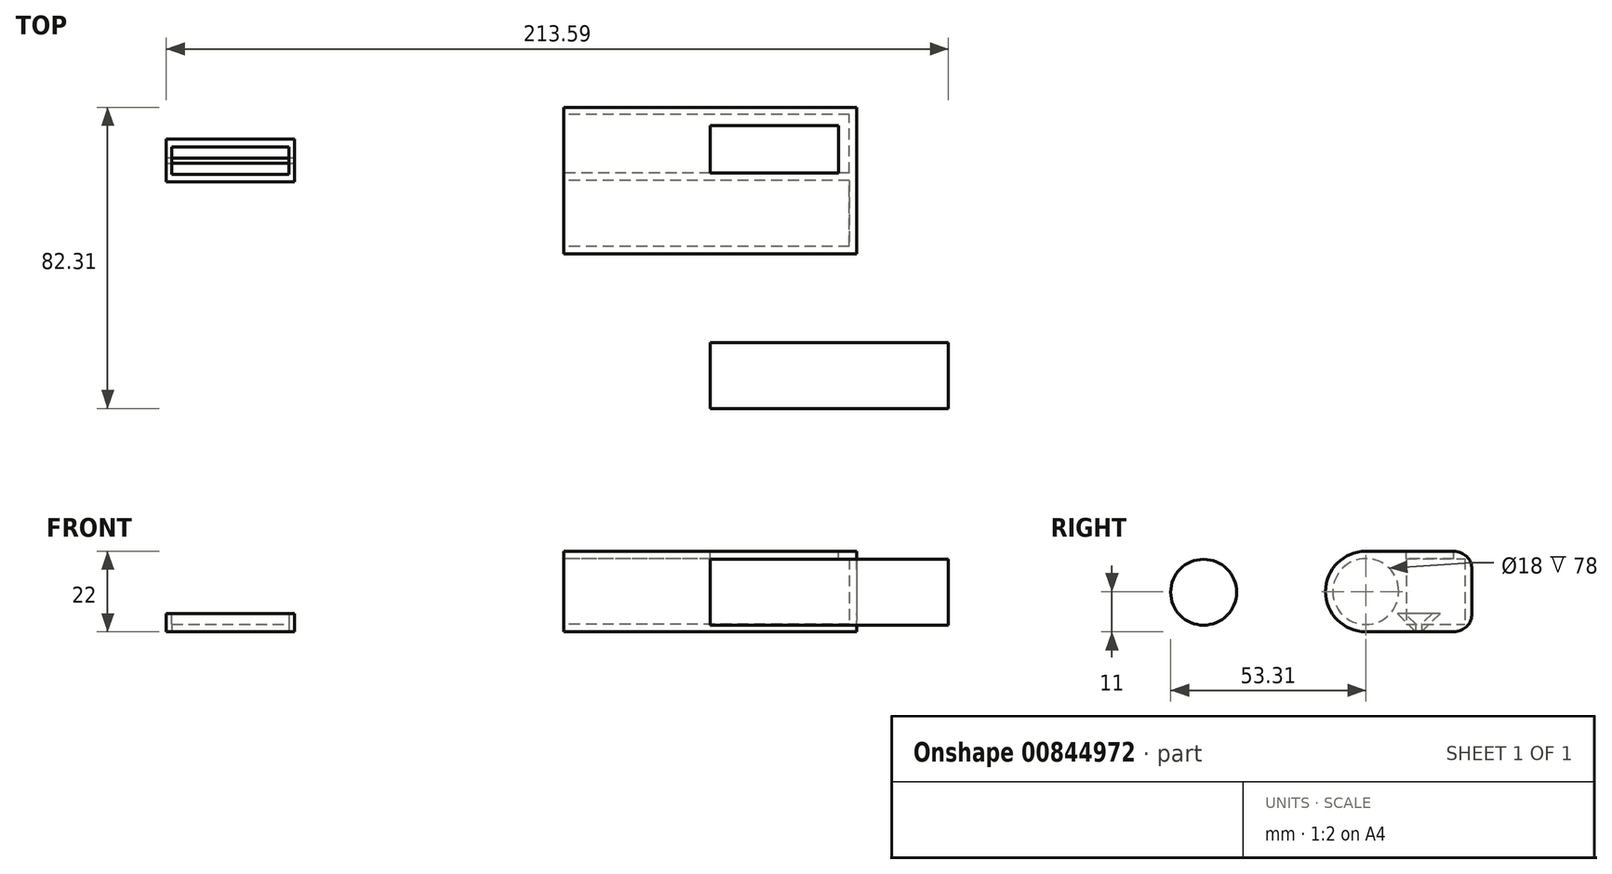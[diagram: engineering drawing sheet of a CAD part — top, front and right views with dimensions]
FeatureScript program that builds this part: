
annotation { "Feature Type Name" : "Feature", "Feature Type Description" : "" }
export const myFeature = defineFeature(function(context is Context, id is Id, definition is map)
    precondition{}
    {
        {
            var Q0;
            Q0=qCreatedBy(makeId("Top.planeOp"),FACE);
            var sketch = newSketch(context, id + "F0", { "sketchPlane" : qUnion([Q0])});
            skLineSegment(sketch, "E0.bottom", {"start": v(40, 20) * mm, "end": v(-40, 20) * mm});
            skLineSegment(sketch, "E0.top", {"start": v(40, -20) * mm, "end": v(-40, -20) * mm});
            skLineSegment(sketch, "E0.left", {"start": v(40, 20) * mm, "end": v(40, -20) * mm});
            skLineSegment(sketch, "E0.right", {"start": v(-40, 20) * mm, "end": v(-40, -20) * mm});
            skPoint(sketch, "E0.middle", {"position": v(0, 0) * mm});
            skSolve(sketch);
        }
        {
            var Q0;
            Q0=makeQuery(id+"F0.imprint","IMPRINT",FACE,{"disambiguationData":[TD([[makeQuery(id+"F0.imprint","IMPRINT",EDGE,{"derivedFrom":sQuery(id+"F0.wireOp",EDGE,"E0.bottom")}),1.0]])]});
            extrude(context, id + "F1", {"entities" : qUnion([Q0]), "depth" : 22 * mm, "offsetDistance" : 25.4 * mm});
        }
        {
            var Q0;
            Q0=makeQuery(id+"F1.opExtrude","CAP_EDGE",EDGE,{"disambiguationData":[OSD([sQuery(id+"F0.wireOp",EDGE,"E0.top")])],"isStart":false});
            var Q1;
            Q1=makeQuery(id+"F1.opExtrude","CAP_EDGE",EDGE,{"disambiguationData":[OSD([sQuery(id+"F0.wireOp",EDGE,"E0.top")])],"isStart":true});
            fillet(context, id + "F2", {"entities" : qUnion([Q0, Q1]), "radius" : 11 * mm, "tangentPropagation" : true, "allowEdgeOverflow" : false});
        }
        {
            var Q0;
            Q0=makeQuery(id+"F1.opExtrude","CAP_FACE",FACE,{"disambiguationData":[OSD([sQuery(id+"F0.wireOp",EDGE,"E0.bottom"),sQuery(id+"F0.wireOp",EDGE,"E0.top"),sQuery(id+"F0.wireOp",EDGE,"E0.left"),sQuery(id+"F0.wireOp",EDGE,"E0.right")])],"isStart":false});
            var sketch = newSketch(context, id + "F3", { "sketchPlane" : qUnion([Q0])});
            skLineSegment(sketch, "E1.bottom", {"start": v(35, 15) * mm, "end": v(0, 15) * mm});
            skLineSegment(sketch, "E1.top", {"start": v(35, 2) * mm, "end": v(0, 2) * mm});
            skLineSegment(sketch, "E1.left", {"start": v(35, 15) * mm, "end": v(35, 2) * mm});
            skLineSegment(sketch, "E1.right", {"start": v(0, 15) * mm, "end": v(0, 2) * mm});
            skPoint(sketch, "E1.middle", {"position": v(17.5, 8.5) * mm});
            skSolve(sketch);
        }
        {
            var Q0;
            Q0 = qSketchRegion(id + "F3", true);
            extrude(context, id + "F4", {"entities" : qUnion([Q0]), "operationType" : NewBodyOperationType.REMOVE, "oppositeDirection" : true, "depth" : 2 * mm, "offsetDistance" : 25.4 * mm});
        }
        {
            var Q0;
            Q0=makeQuery(id+"F1.opExtrude","CAP_EDGE",EDGE,{"disambiguationData":[OSD([sQuery(id+"F0.wireOp",EDGE,"E0.bottom")])],"isStart":false});
            var Q1;
            Q1=makeQuery(id+"F1.opExtrude","CAP_EDGE",EDGE,{"disambiguationData":[OSD([sQuery(id+"F0.wireOp",EDGE,"E0.bottom")])],"isStart":true});
            fillet(context, id + "F5", {"entities" : qUnion([Q0, Q1]), "radius" : 5 * mm, "tangentPropagation" : true, "allowEdgeOverflow" : false});
        }
        {
            var Q0;
            Q0=qCreatedBy(makeId("Top.planeOp"),FACE);
            var sketch = newSketch(context, id + "F6", { "sketchPlane" : qUnion([Q0])});
            skLineSegment(sketch, "E2.bottom", {"start": v(-113.6, 11.36) * mm, "end": v(-148.6, 11.36) * mm});
            skLineSegment(sketch, "E2.top", {"start": v(-113.6, -0.5) * mm, "end": v(-148.6, -0.5) * mm});
            skLineSegment(sketch, "E2.left", {"start": v(-113.6, 11.36) * mm, "end": v(-113.6, -0.5) * mm});
            skLineSegment(sketch, "E2.right", {"start": v(-148.6, 11.36) * mm, "end": v(-148.6, -0.5) * mm});
            skPoint(sketch, "E2.middle", {"position": v(-131.1, 5.43) * mm});
            skSolve(sketch);
        }
        {
            var Q0;
            Q0=makeQuery(id+"F6.imprint","IMPRINT",FACE,{"disambiguationData":[TD([[makeQuery(id+"F6.imprint","IMPRINT",EDGE,{"derivedFrom":sQuery(id+"F6.wireOp",EDGE,"E2.bottom")}),1.0]])]});
            extrude(context, id + "F7", {"entities" : qUnion([Q0]), "depth" : 5 * mm, "offsetDistance" : 25.4 * mm});
        }
        {
            var Q0;
            Q0=makeQuery(id+"F7.opExtrude","CAP_EDGE",EDGE,{"disambiguationData":[OSD([sQuery(id+"F6.wireOp",EDGE,"E2.top")])],"isStart":true});
            var Q1;
            Q1=makeQuery(id+"F7.opExtrude","CAP_EDGE",EDGE,{"disambiguationData":[OSD([sQuery(id+"F6.wireOp",EDGE,"E2.bottom")])],"isStart":true});
            chamfer(context, id + "F8", {"entities" : qUnion([Q0, Q1]), "width" : 5.08 * mm});
        }
        {
            var Q0;
            Q0=makeQuery(id+"F7.opExtrude","CAP_FACE",FACE,{"disambiguationData":[OSD([sQuery(id+"F6.wireOp",EDGE,"E2.bottom"),sQuery(id+"F6.wireOp",EDGE,"E2.top"),sQuery(id+"F6.wireOp",EDGE,"E2.left"),sQuery(id+"F6.wireOp",EDGE,"E2.right")])],"isStart":false});
            shell(context, id + "F9", {"entities" : qUnion([Q0]), "thickness" : 1.5 * mm});
        }
        {
            var Q0;
            Q0=makeQuery(id+"F7.opExtrude","CAP_FACE",FACE,{"disambiguationData":[OSD([sQuery(id+"F6.wireOp",EDGE,"E2.bottom"),sQuery(id+"F6.wireOp",EDGE,"E2.top"),sQuery(id+"F6.wireOp",EDGE,"E2.left"),sQuery(id+"F6.wireOp",EDGE,"E2.right")])],"isStart":true});
            var sketch = newSketch(context, id + "F10", { "sketchPlane" : qUnion([Q0])});
            skLineSegment(sketch, "E3.bottom", {"start": v(-115.1, -6.28) * mm, "end": v(-147.1, -6.28) * mm});
            skLineSegment(sketch, "E3.top", {"start": v(-115.1, -4.58) * mm, "end": v(-147.1, -4.58) * mm});
            skLineSegment(sketch, "E3.left", {"start": v(-115.1, -6.28) * mm, "end": v(-115.1, -4.58) * mm});
            skLineSegment(sketch, "E3.right", {"start": v(-147.1, -6.28) * mm, "end": v(-147.1, -4.58) * mm});
            skPoint(sketch, "E3.middle", {"position": v(-131.1, -5.43) * mm});
            skPoint(sketch, "E3.middle.positionSnap0", {"position": v(-131.1, -6.28) * mm});
            skPoint(sketch, "E3.centerSnap0", {"position": v(-131.1, -6.28) * mm});
            skSolve(sketch);
        }
        {
            var Q0;
            Q0 = qSketchRegion(id + "F10", true);
            extrude(context, id + "F11", {"entities" : qUnion([Q0]), "operationType" : NewBodyOperationType.REMOVE, "oppositeDirection" : true, "depth" : 2 * mm, "offsetDistance" : 25.4 * mm});
        }
        {
            var Q0;
            Q0=qCreatedBy(makeId("Right.planeOp"),FACE);
            var sketch = newSketch(context, id + "F12", { "sketchPlane" : qUnion([Q0])});
            skCircle(sketch, "E4", {"center": v(-53.3, 10.8) * mm, "radius": 9 * mm});
            skSolve(sketch);
        }
        {
            var Q0;
            Q0 = qSketchRegion(id + "F12", true);
            extrude(context, id + "F13", {"entities" : qUnion([Q0]), "depth" : 65 * mm, "offsetDistance" : 25.4 * mm});
        }
        {
            var Q0;
            Q0=makeQuery(id+"F1.opExtrude","SWEPT_FACE",FACE,{"disambiguationData":[OSD([sQuery(id+"F0.wireOp",EDGE,"E0.right")])]});
            var sketch = newSketch(context, id + "F14", { "sketchPlane" : qUnion([Q0])});
            skCircle(sketch, "E5", {"center": v(9, 11) * mm, "radius": 9 * mm});
            skSolve(sketch);
        }
        {
            var Q0;
            Q0=makeQuery(id+"F14.imprint","IMPRINT",FACE,{"disambiguationData":[TD([[makeQuery(id+"F14.imprint","IMPRINT",EDGE,{"derivedFrom":sQuery(id+"F14.wireOp",EDGE,"E5")}),1.0]])]});
            extrude(context, id + "F15", {"entities" : qUnion([Q0]), "operationType" : NewBodyOperationType.REMOVE, "oppositeDirection" : true, "depth" : 78 * mm, "offsetDistance" : 25.4 * mm});
        }
        {
            var Q0;
            Q0=makeQuery(id+"F1.opExtrude","SWEPT_FACE",FACE,{"disambiguationData":[OSD([sQuery(id+"F0.wireOp",EDGE,"E0.right")])]});
            var sketch = newSketch(context, id + "F16", { "sketchPlane" : qUnion([Q0])});
            skLineSegment(sketch, "E6.bottom", {"start": v(-2, 20) * mm, "end": v(-18, 20) * mm});
            skLineSegment(sketch, "E6.top", {"start": v(-2, 2) * mm, "end": v(-18, 2) * mm});
            skLineSegment(sketch, "E6.left", {"start": v(-2, 20) * mm, "end": v(-2, 2) * mm});
            skLineSegment(sketch, "E6.right", {"start": v(-18, 20) * mm, "end": v(-18, 2) * mm});
            skPoint(sketch, "E6.middle", {"position": v(-10, 11) * mm});
            skSolve(sketch);
        }
        {
            var Q0;
            Q0 = qSketchRegion(id + "F16", true);
            extrude(context, id + "F17", {"entities" : qUnion([Q0]), "operationType" : NewBodyOperationType.REMOVE, "oppositeDirection" : true, "depth" : 78 * mm, "offsetDistance" : 25.4 * mm});
        }
    });
